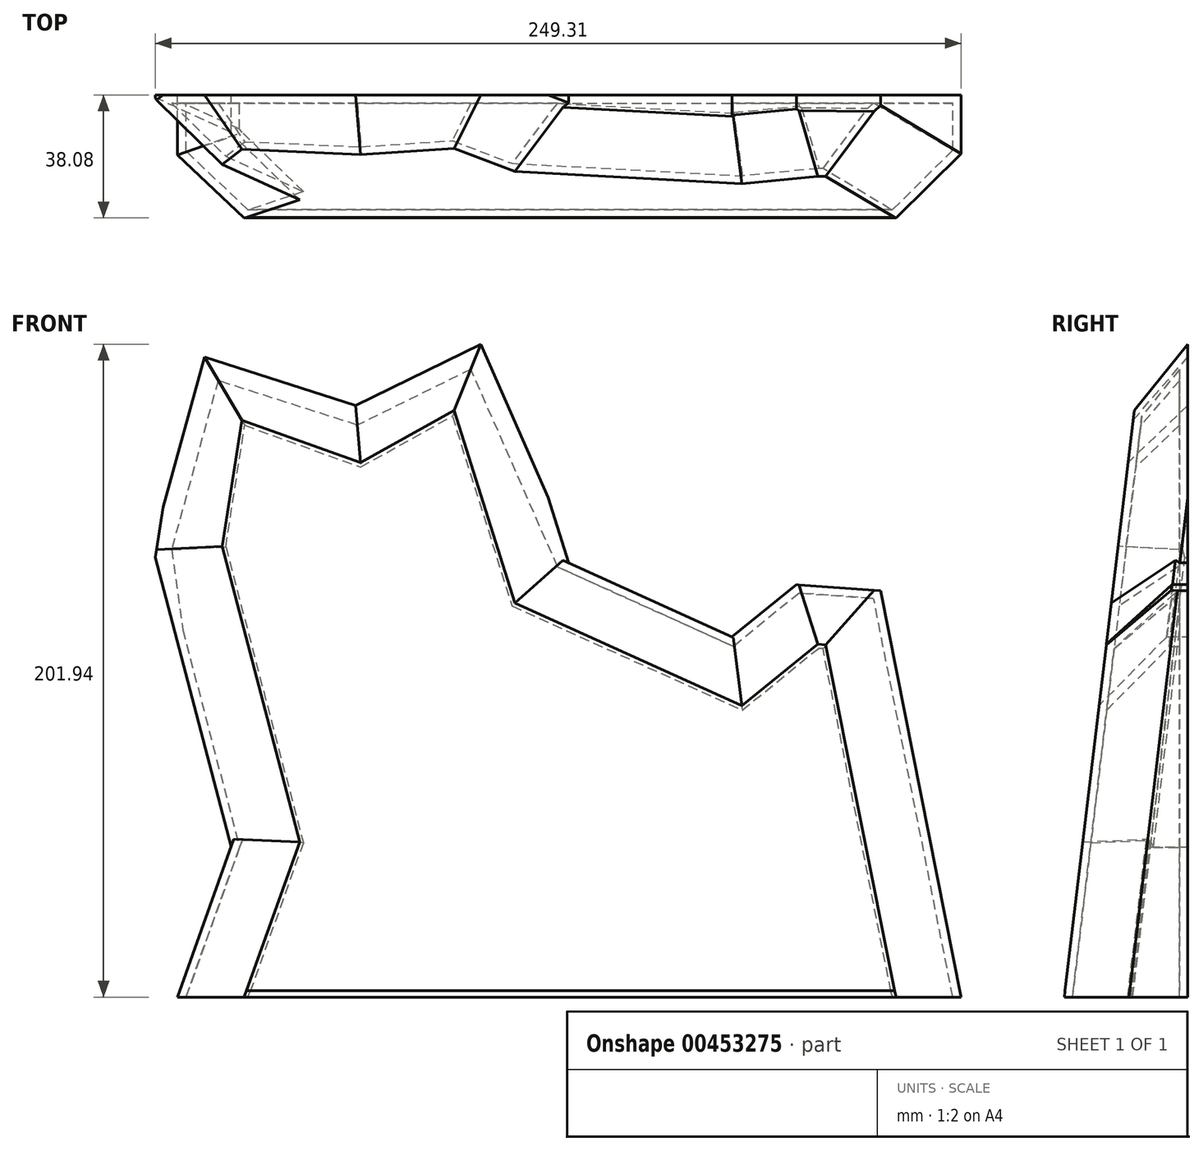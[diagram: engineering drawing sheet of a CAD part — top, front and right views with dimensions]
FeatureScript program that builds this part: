
annotation { "Feature Type Name" : "Feature", "Feature Type Description" : "" }
export const myFeature = defineFeature(function(context is Context, id is Id, definition is map)
    precondition{}
    {
        {
            var Q0;
            Q0=qCreatedBy(makeId("Front.planeOp"),FACE);
            var sketch = newSketch(context, id + "F0", { "sketchPlane" : qUnion([Q0])});
            skLineSegment(sketch, "E0", {"start": v(143.16, 65.23) * mm, "end": v(153.65, 132.78) * mm});
            skLineSegment(sketch, "E1", {"start": v(153.65, 132.78) * mm, "end": v(204.8, 114.42) * mm});
            skLineSegment(sketch, "E2", {"start": v(204.8, 114.42) * mm, "end": v(247.58, 138.2) * mm});
            skLineSegment(sketch, "E3", {"start": v(247.58, 138.2) * mm, "end": v(271.05, 63.6) * mm});
            skLineSegment(sketch, "E4", {"start": v(271.05, 63.6) * mm, "end": v(321.63, 40.73) * mm});
            skLineSegment(sketch, "E5", {"start": v(143.16, 65.23) * mm, "end": v(166.6, -24.2) * mm});
            skLineSegment(sketch, "E6", {"start": v(166.6, -24.2) * mm, "end": v(149.96, -70.68) * mm});
            skLineSegment(sketch, "E7", {"start": v(149.96, -70.68) * mm, "end": v(392.47, -70.68) * mm});
            skLineSegment(sketch, "E8", {"start": v(392.47, -70.68) * mm, "end": v(367.52, 55.02) * mm});
            skLineSegment(sketch, "E9", {"start": v(367.52, 55.02) * mm, "end": v(341.55, 56.87) * mm});
            skLineSegment(sketch, "E10", {"start": v(341.55, 56.87) * mm, "end": v(321.63, 40.73) * mm});
            skLineSegment(sketch, "E11", {"start": v(423.35, 18.03) * mm, "end": v(398.43, 60.66) * mm});
            skLineSegment(sketch, "E12", {"start": v(398.43, 60.66) * mm, "end": v(416.14, 80.99) * mm});
            skLineSegment(sketch, "E13", {"start": v(416.14, 80.99) * mm, "end": v(439.48, 60.66) * mm});
            skLineSegment(sketch, "E14", {"start": v(439.48, 60.66) * mm, "end": v(490.9, 60.66) * mm});
            skLineSegment(sketch, "E15", {"start": v(490.9, 60.66) * mm, "end": v(511.9, 72.46) * mm});
            skLineSegment(sketch, "E16", {"start": v(511.9, 72.46) * mm, "end": v(519.1, 86.9) * mm});
            skLineSegment(sketch, "E17", {"start": v(519.1, 86.9) * mm, "end": v(535.37, 78.76) * mm});
            skLineSegment(sketch, "E18", {"start": v(535.37, 78.76) * mm, "end": v(542.72, 60.66) * mm});
            skLineSegment(sketch, "E19", {"start": v(542.72, 60.66) * mm, "end": v(528.29, 33.77) * mm});
            skLineSegment(sketch, "E20", {"start": v(528.29, 33.77) * mm, "end": v(508.61, 18.68) * mm});
            skLineSegment(sketch, "E21", {"start": v(508.61, 18.68) * mm, "end": v(527.63, -70.68) * mm});
            skLineSegment(sketch, "E22", {"start": v(527.63, -70.68) * mm, "end": v(408.27, -70.68) * mm});
            skLineSegment(sketch, "E23", {"start": v(408.27, -70.68) * mm, "end": v(423.35, 18.03) * mm});
            skSolve(sketch);
        }
        {
            var Q0;
            Q0=makeQuery(id+"F0.imprint","IMPRINT",FACE,{"disambiguationData":[TD([[makeQuery(id+"F0.imprint","IMPRINT",EDGE,{"derivedFrom":sQuery(id+"F0.wireOp",EDGE,"E0")}),-1.0]])]});
            extrude(context, id + "F1", {"entities" : qUnion([Q0]), "depth" : 38.1 * mm});
        }
        {
            var Q0;
            Q0=qCreatedBy(makeId("Right.planeOp"),FACE);
            cPlane(context, id + "F2", {"entities" : qUnion([Q0]), "cplaneType" : CPlaneType.OFFSET, "offset" : 76.2 * mm, "oppositeDirection" : true, "width" : 152.4 * mm, "height" : 152.4 * mm});
        }
        {
            var Q0;
            Q0=qCreatedBy(id+"F2.planeOp",FACE);
            var sketch = newSketch(context, id + "F3", { "sketchPlane" : qUnion([Q0])});
            skLineSegment(sketch, "E24", {"start": v(-38.19, -70.6) * mm, "end": v(0, 248.97) * mm});
            skLineSegment(sketch, "E25", {"start": v(0, 248.97) * mm, "end": v(-45.77, 254.44) * mm});
            skLineSegment(sketch, "E26", {"start": v(-45.77, 254.44) * mm, "end": v(-38.19, -70.6) * mm});
            skSolve(sketch);
        }
        {
            var Q0;
            Q0=qSketchRegion(id+"F3",true);
            extrude(context, id + "F4", {"entities" : qUnion([Q0]), "operationType" : NewBodyOperationType.REMOVE, "endBound" : BoundingType.THROUGH_ALL, "depth" : 25.4 * mm});
        }
        {
            var Q0;
            Q0=makeQuery(id+"F4.boolean.opBoolean","COPY",FACE,{"derivedFrom":makeQuery(id+"F4.opExtrude","SWEPT_FACE",FACE,{"disambiguationData":[OSD([sQuery(id+"F3.wireOp",EDGE,"E24")])]})});
            chamfer(context, id + "F5", {"entities" : qUnion([Q0]), "width" : 20.32 * mm, "tangentPropagation" : true});
        }
        {
            var Q0;
            Q0=makeQuery(id+"F1.opExtrude","SWEPT_FACE",FACE,{"disambiguationData":[OSD([sQuery(id+"F0.wireOp",EDGE,"5UBScBti-lYJG-QWJU-C9wr-LBJ0cxTIyK4E")])]});
            var Q1;
            Q1=makeQuery(id+"F1.opExtrude","SWEPT_FACE",FACE,{"disambiguationData":[OSD([sQuery(id+"F0.wireOp",EDGE,"E7")])]});
            shell(context, id + "F6", {"entities" : qUnion([Q0, Q1]), "thickness" : 2.54 * mm});
        }
    });
